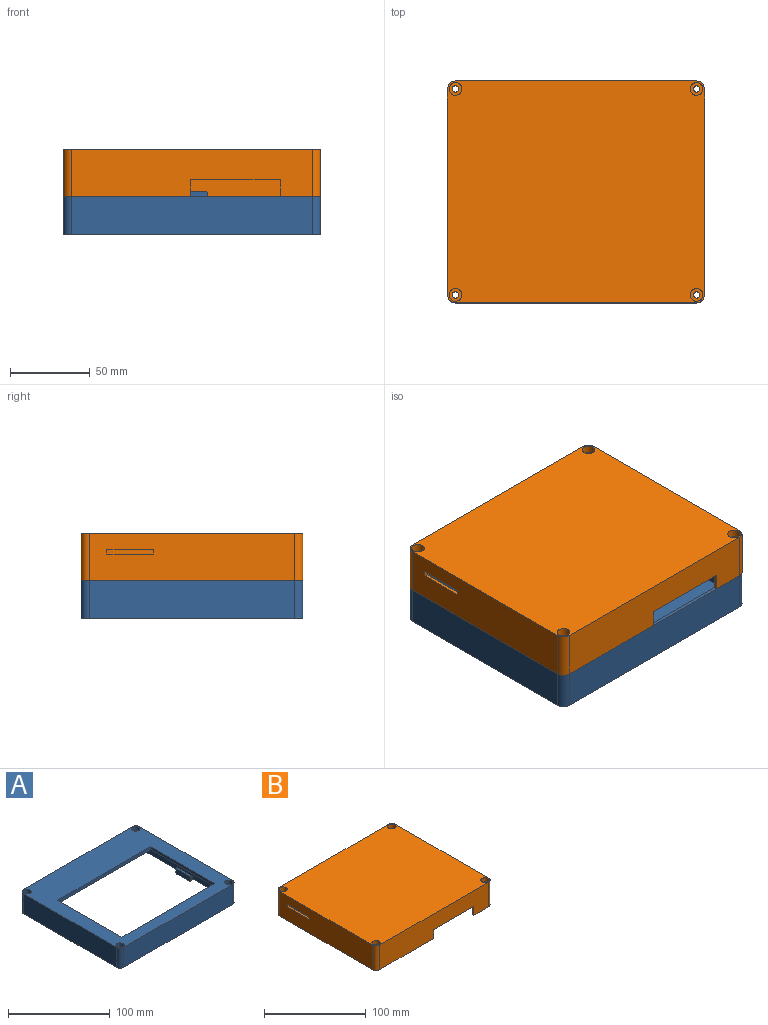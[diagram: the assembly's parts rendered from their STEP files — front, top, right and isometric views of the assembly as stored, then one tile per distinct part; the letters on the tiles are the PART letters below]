
ASSEMBLY  parts=2 mates=1
PART A: 79 faces, bbox 161x139x27 mm
  f0: plane 161x139mm, normal (0,0,1), area 10675.5mm2, adj f5,f6,f7,f8,f15,f17,f19,f21
  f1: plane 157x135mm, normal (0,0,-1), area 9309.1mm2, adj f2,f3,f9,f10,f11,f12,f13,f14
  f2: plane 143x20mm, normal (0,-1,0), area 2798.8mm2, adj f1,f4,f13,f14,f41,f55,f56
  f3: plane 121x20mm, normal (1,0,0), area 2349.2mm2, adj f1,f4,f12,f14,f35,f61,f62
  f4: plane 161x139mm, normal (0,0,-1), area 1344.7mm2, adj f2,f3,f5,f6,f7,f8,f9,f10
  f5: plane 129x24mm, normal (-1,0,0), area 3096mm2, adj f0,f4,f27,f30
  f6: plane 151x24mm, normal (0,-1,0), area 3624mm2, adj f0,f4,f27,f28
  f7: plane 129x24mm, normal (1,0,0), area 3096mm2, adj f0,f4,f28,f29
  f8: plane 151x24mm, normal (0,1,0), area 3624mm2, adj f0,f4,f29,f30
  f9: plane 121x20mm, normal (-1,0,0), area 2349.2mm2, adj f1,f4,f11,f13,f47,f59,f60
  f10: plane 143x20mm, normal (0,1,0), area 2789.2mm2, adj f1,f4,f11,f12,f53,f57,f58
  f11: cylinder r=5mm len=20mm, axis (0,0,1), area 285.8mm2, adj f1,f4,f9,f10
  f12: cylinder r=5mm len=20mm, axis (0,0,1), area 285.8mm2, adj f1,f3,f4,f10
  f13: cylinder r=5mm len=20mm, axis (0,0,1), area 285.8mm2, adj f1,f2,f4,f9
  f14: cylinder r=5mm len=20mm, axis (0,0,1), area 285.8mm2, adj f1,f2,f3,f4
  f15: cylinder r=4mm len=8mm, axis (0,0,1), area 125.7mm2, adj f0,f16
  f16: plane 8x8mm, normal (0,0,1), area 37.7mm2, adj f15,f23
  f17: cylinder r=4mm len=8mm, axis (0,0,1), area 125.7mm2, adj f0,f18
  f18: plane 8x8mm, normal (0,0,1), area 37.7mm2, adj f17,f24
  f19: cylinder r=4mm len=8mm, axis (0,0,1), area 125.7mm2, adj f0,f20
  f20: plane 8x8mm, normal (0,0,1), area 37.7mm2, adj f19,f25
  f21: cylinder r=4mm len=8mm, axis (0,0,1), area 125.7mm2, adj f0,f22
  f22: plane 8x8mm, normal (0,0,1), area 37.7mm2, adj f21,f26
  f23: cylinder r=2mm len=19mm, axis (0,0,1), area 238.8mm2, adj f4,f16
  f24: cylinder r=2mm len=19mm, axis (0,0,1), area 238.8mm2, adj f4,f18
  f25: cylinder r=2mm len=19mm, axis (0,0,1), area 238.8mm2, adj f4,f20
  f26: cylinder r=2mm len=19mm, axis (0,0,1), area 238.8mm2, adj f4,f22
  f27: cylinder r=5mm len=24mm, axis (0,0,1), area 188.5mm2, adj f0,f4,f5,f6
  f28: cylinder r=5mm len=24mm, axis (0,0,-1), area 188.5mm2, adj f0,f4,f6,f7
  f29: cylinder r=5mm len=24mm, axis (0,0,1), area 188.5mm2, adj f0,f4,f7,f8
  f30: cylinder r=5mm len=24mm, axis (0,0,-1), area 188.5mm2, adj f0,f4,f5,f8
  f31: plane 4.6x2mm, normal (0,-1,0), area 3.8mm2, adj f4,f32,f34,f35,f62,f70
  f32: plane 20x1.6mm, normal (-1,0,0), area 32mm2, adj f4,f31,f33,f72
  f33: plane 4.6x2mm, normal (0,1,0), area 3.8mm2, adj f4,f32,f34,f35,f61,f71
  f34: plane 20x6mm, normal (1,0,0), area 119.2mm2, adj f31,f33,f35,f36,f70,f71
  f35: plane 23.6x2mm, normal (0,0,1), area 41.4mm2, adj f3,f31,f33,f34,f61,f62
  f36: plane 17.2x0.6mm, normal (0,0,-1), area 10.3mm2, adj f34,f70,f71,f72
  f37: plane 6x2mm, normal (-1,0,0), area 6.2mm2, adj f4,f38,f40,f41,f42,f56,f63
  f38: plane 16.79x1.6mm, normal (0,1,0), area 26.9mm2, adj f4,f37,f39,f63
  f39: plane 6x2mm, normal (1,0,0), area 6.2mm2, adj f4,f38,f40,f41,f42,f55,f63
  f40: plane 16.79x6mm, normal (0,-1,0), area 100.7mm2, adj f37,f39,f41,f42
  f41: plane 20.39x2mm, normal (0,0,1), area 35mm2, adj f2,f37,f39,f40,f55,f56
  f42: plane 16.79x0.6mm, normal (0,0,-1), area 10.1mm2, adj f37,f39,f40,f63
  f43: plane 4.6x2mm, normal (0,1,0), area 3.8mm2, adj f4,f44,f46,f47,f59,f67
  f44: plane 20x1.6mm, normal (1,0,0), area 32mm2, adj f4,f43,f45,f68
  f45: plane 4.6x2mm, normal (0,-1,0), area 3.8mm2, adj f4,f44,f46,f47,f60,f69
  f46: plane 20x6mm, normal (-1,0,0), area 119.2mm2, adj f43,f45,f47,f48,f67,f69
  f47: plane 23.6x2mm, normal (0,0,1), area 41.4mm2, adj f9,f43,f45,f46,f59,f60
  f48: plane 17.2x0.6mm, normal (0,0,-1), area 10.3mm2, adj f46,f67,f68,f69
  f49: plane 20x1.6mm, normal (0,-1,0), area 32mm2, adj f4,f50,f52,f65
  f50: plane 4.6x2mm, normal (-1,0,0), area 3.8mm2, adj f4,f49,f51,f53,f58,f66
  f51: plane 20x6mm, normal (0,1,0), area 119.2mm2, adj f50,f52,f53,f54,f64,f66
  f52: plane 4.6x2mm, normal (1,0,0), area 3.8mm2, adj f4,f49,f51,f53,f57,f64
  f53: plane 23.6x2mm, normal (0,0,1), area 41.4mm2, adj f10,f50,f51,f52,f57,f58
  f54: plane 17.2x0.6mm, normal (0,0,-1), area 10.3mm2, adj f51,f64,f65,f66
  f55: cylinder r=1.8mm len=3mm, axis (0,0,-1), area 8.5mm2, adj f2,f4,f39,f41
  f56: cylinder r=1.8mm len=3mm, axis (0,0,1), area 8.5mm2, adj f2,f4,f37,f41
  f57: cylinder r=1.8mm len=3mm, axis (0,0,-1), area 8.5mm2, adj f4,f10,f52,f53
  f58: cylinder r=1.8mm len=3mm, axis (0,0,1), area 8.5mm2, adj f4,f10,f50,f53
  f59: cylinder r=1.8mm len=3mm, axis (0,0,-1), area 8.5mm2, adj f4,f9,f43,f47
  f60: cylinder r=1.8mm len=3mm, axis (0,0,1), area 8.5mm2, adj f4,f9,f45,f47
  f61: cylinder r=1.8mm len=3mm, axis (0,0,-1), area 8.5mm2, adj f3,f4,f33,f35
  f62: cylinder r=1.8mm len=3mm, axis (0,0,1), area 8.5mm2, adj f3,f4,f31,f35
  f63: cylinder r=1.4mm len=16.79mm, axis (1,0,0), area 36.9mm2, adj f37,f38,f39,f42
  f64: cylinder r=1.4mm len=2mm, axis (0,-1,0), area 3.3mm2, adj f51,f52,f54,f65
  f65: cylinder r=1.4mm len=20mm, axis (-1,0,0), area 41.7mm2, adj f49,f54,f64,f66
  f66: cylinder r=1.4mm len=2mm, axis (0,1,0), area 3.3mm2, adj f50,f51,f54,f65
  f67: cylinder r=1.4mm len=2mm, axis (1,0,0), area 3.3mm2, adj f43,f46,f48,f68
  f68: cylinder r=1.4mm len=20mm, axis (0,-1,0), area 41.7mm2, adj f44,f48,f67,f69
  f69: cylinder r=1.4mm len=2mm, axis (-1,0,0), area 3.3mm2, adj f45,f46,f48,f68
  f70: cylinder r=1.4mm len=2mm, axis (-1,0,0), area 3.3mm2, adj f31,f34,f36,f72
  f71: cylinder r=1.4mm len=2mm, axis (1,0,0), area 3.3mm2, adj f33,f34,f36,f72
  f72: cylinder r=1.4mm len=20mm, axis (0,1,0), area 41.7mm2, adj f32,f36,f70,f71
  f73: plane 131x4mm, normal (0,-1,0), area 516.5mm2, adj f0,f1,f74,f76,f77,f78
  f74: plane 89x3.5mm, normal (1,0,0), area 311.5mm2, adj f0,f73,f75,f77
  f75: plane 131x4mm, normal (0,1,0), area 516.5mm2, adj f0,f1,f74,f76,f77,f78
  f76: plane 89x3.5mm, normal (-1,0,0), area 311.5mm2, adj f0,f73,f75,f78
  f77: plane 89x1mm, normal (0.45,0,-0.89), area 99.5mm2, adj f1,f73,f74,f75
  f78: plane 89x1mm, normal (-0.45,0,-0.89), area 99.5mm2, adj f1,f73,f75,f76
PART B: 65 faces, bbox 161x139x29.5 mm
  f0: plane 151x29.5mm, normal (0,1,0), area 4076.6mm2, adj f3,f6,f9,f29,f30,f56,f57,f58
  f1: plane 143x27.5mm, normal (0,-1,0), area 3554.6mm2, adj f3,f6,f13,f14,f56,f57,f58,f59
  f2: plane 143x27.5mm, normal (0,1,0), area 3335.5mm2, adj f3,f6,f11,f12,f45,f46,f47,f48
  f3: plane 157x137mm, normal (0,0,-1), area 18995.6mm2, adj f0,f1,f2,f4,f10,f11,f12,f13
  f4: plane 121x27.5mm, normal (1,0,0), area 2987.9mm2, adj f3,f6,f12,f14,f31,f32,f33,f34
  f5: plane 129x29.5mm, normal (-1,0,0), area 3715mm2, adj f6,f9,f27,f30,f31,f32,f33,f34
  f6: plane 161x139mm, normal (0,0,-1), area 1227.2mm2, adj f0,f1,f2,f4,f5,f7,f8,f10
  f7: plane 151x29.5mm, normal (0,-1,0), area 3866.5mm2, adj f6,f9,f27,f28,f45,f46,f47
  f8: plane 129x29.5mm, normal (1,0,0), area 3805.5mm2, adj f6,f9,f28,f29
  f9: plane 161x139mm, normal (0,0,1), area 22156.5mm2, adj f0,f5,f7,f8,f15,f17,f19,f21
  f10: plane 121x27.5mm, normal (-1,0,0), area 3327.5mm2, adj f3,f6,f11,f13
  f11: cylinder r=5mm len=27.5mm, axis (0,0,1), area 392.9mm2, adj f2,f3,f6,f10
  f12: cylinder r=5mm len=27.5mm, axis (0,0,1), area 392.9mm2, adj f2,f3,f4,f6
  f13: cylinder r=5mm len=27.5mm, axis (0,0,1), area 392.9mm2, adj f1,f3,f6,f10
  f14: cylinder r=5mm len=27.5mm, axis (0,0,1), area 392.9mm2, adj f1,f3,f4,f6
  f15: cylinder r=4mm len=8mm, axis (0,0,1), area 125.7mm2, adj f9,f16
  f16: plane 8x8mm, normal (0,0,1), area 37.7mm2, adj f15,f23
  f17: cylinder r=4mm len=8mm, axis (0,0,1), area 125.7mm2, adj f9,f18
  f18: plane 8x8mm, normal (0,0,1), area 37.7mm2, adj f17,f24
  f19: cylinder r=4mm len=8mm, axis (0,0,1), area 125.7mm2, adj f9,f20
  f20: plane 8x8mm, normal (0,0,1), area 37.7mm2, adj f19,f25
  f21: cylinder r=4mm len=8mm, axis (0,0,1), area 125.7mm2, adj f9,f22
  f22: plane 8x8mm, normal (0,0,1), area 37.7mm2, adj f21,f26
  f23: cylinder r=2mm len=24.5mm, axis (0,0,1), area 307.9mm2, adj f6,f16
  f24: cylinder r=2mm len=24.5mm, axis (0,0,1), area 307.9mm2, adj f6,f18
  f25: cylinder r=2mm len=24.5mm, axis (0,0,1), area 307.9mm2, adj f6,f20
  f26: cylinder r=2mm len=24.5mm, axis (0,0,1), area 307.9mm2, adj f6,f22
  f27: cylinder r=5mm len=29.5mm, axis (0,0,1), area 231.7mm2, adj f5,f6,f7,f9
  f28: cylinder r=5mm len=29.5mm, axis (0,0,-1), area 231.7mm2, adj f6,f7,f8,f9
  f29: cylinder r=5mm len=29.5mm, axis (0,0,1), area 231.7mm2, adj f0,f6,f8,f9
  f30: cylinder r=5mm len=29.5mm, axis (0,0,-1), area 231.7mm2, adj f0,f5,f6,f9
  f31: plane 3.1x2mm, normal (0,1,0), area 6.2mm2, adj f4,f5,f32,f34
  f32: plane 29.2x2mm, normal (0,0,-1), area 58.4mm2, adj f4,f5,f31,f33
  f33: plane 3.1x2mm, normal (0,-1,0), area 6.2mm2, adj f4,f5,f32,f34
  f34: plane 29.2x2mm, normal (0,0,1), area 58.4mm2, adj f4,f5,f31,f33
  f35: plane 49.5x4mm, normal (0,-1,0), area 198mm2, adj f4,f36,f42,f43
  f36: plane 49.5x32mm, normal (0,0,-1), area 1580.5mm2, adj f4,f35,f37,f42,f61,f63
  f37: plane 49.5x4mm, normal (0,1,0), area 198mm2, adj f4,f36,f42,f44
  f38: plane 49.5x0.5mm, normal (0,0,-1), area 24.8mm2, adj f4,f40,f42,f44
  f39: plane 49.5x0.5mm, normal (0,0,-1), area 24.8mm2, adj f4,f41,f42,f43
  f40: plane 49.5x11.7mm, normal (0,-1,0), area 579.1mm2, adj f3,f4,f38,f42
  f41: plane 49.5x11.7mm, normal (0,1,0), area 579.1mm2, adj f3,f4,f39,f42
  f42: plane 35x11.7mm, normal (1,0,0), area 249.1mm2, adj f3,f35,f36,f37,f38,f39,f40,f41
  f43: cylinder r=1mm len=49.5mm, axis (-1,0,0), area 77.8mm2, adj f4,f35,f39,f42
  f44: cylinder r=1mm len=49.5mm, axis (-1,0,0), area 77.8mm2, adj f4,f37,f38,f42
  f45: plane 10.5x2mm, normal (-1,0,0), area 21mm2, adj f2,f6,f7,f47
  f46: plane 10.5x2mm, normal (1,0,0), area 21mm2, adj f2,f6,f7,f47
  f47: plane 56x2mm, normal (0,0,-1), area 112mm2, adj f2,f7,f45,f46
  f48: plane 98x3mm, normal (1,0,0), area 294mm2, adj f2,f3,f49,f51
  f49: plane 3x1.5mm, normal (0,1,0), area 4.5mm2, adj f3,f48,f50,f51
  f50: plane 98x3mm, normal (-1,0,0), area 294mm2, adj f2,f3,f49,f51
  f51: plane 98x1.5mm, normal (0,0,-1), area 147mm2, adj f2,f48,f49,f50
  f52: plane 98x3mm, normal (-1,0,0), area 294mm2, adj f2,f3,f54,f55
  f53: plane 98x3mm, normal (1,0,0), area 294mm2, adj f2,f3,f54,f55
  f54: plane 3x1.5mm, normal (0,1,0), area 4.5mm2, adj f3,f52,f53,f55
  f55: plane 98x1.5mm, normal (0,0,-1), area 147mm2, adj f2,f52,f53,f54
  f56: plane 26x2mm, normal (0,0,1), area 52mm2, adj f0,f1,f59,f60
  f57: plane 13.5x2mm, normal (1,0,0), area 27mm2, adj f0,f1,f3,f59
  f58: plane 13.5x2mm, normal (-1,0,0), area 27mm2, adj f0,f1,f3,f60
  f59: cylinder r=0.5mm len=2mm, axis (0,1,0), area 1.6mm2, adj f0,f1,f56,f57
  f60: cylinder r=0.5mm len=2mm, axis (0,-1,0), area 1.6mm2, adj f0,f1,f56,f58
  f61: cylinder r=0.75mm len=5.2mm, axis (0,0,-1), area 24.5mm2, adj f36,f62
  f62: plane 1.5x1.5mm, normal (0,0,-1), area 1.8mm2, adj f61
  f63: cylinder r=0.75mm len=5.2mm, axis (0,0,-1), area 24.5mm2, adj f36,f64
  f64: plane 1.5x1.5mm, normal (0,0,-1), area 1.8mm2, adj f63
PLACE A rot(axis=(1,0,0),180deg) t=(-0.07,125.07,2.7)mm
PLACE B t=(-0.07,-13.93,2.7)mm
MATE fastened B.f11 <-> A.f13  axis (0,0,-1) through (155.93,-8.93,2.7)mm
